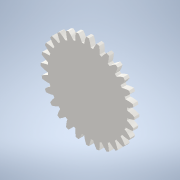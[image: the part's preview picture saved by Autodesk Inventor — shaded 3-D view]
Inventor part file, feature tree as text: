
AUTODESK INVENTOR PART (.ipt)
format: ipt  version: 2022 (Build 260153000, 153)  size: 248,320 bytes
history: native  units: mm (DEFAULTED — no unit token found)
features: plane x3, other x3, sketch x2, extrude x1
ambient origin geometry x8: Origin, YZ Plane, XZ Plane, XY Plane, X Axis, Y Axis, Z Axis, Center Point
bodies: Solid1 (feature_tree)
feature tree (9):
  extrude  "Extrusion1"  Depth=4.0mm TaperAngle=0.0deg
  plane  "Work Plane2"
  plane  "Work Plane8"
  plane  "Work Plane9"
  other  "Spur Gear"
  sketch  "Sketch1"  dims[d0=74.902823mm d1=4.0mm d2=0.0mm]
  sketch  "Sketch2"  dims[d3=70.0mm d4=10.0mm d5=0.0mm d16=70.971478mm d17=0.0mm d34=1.121997mm d39=0.0mm d41=0.0mm d43=70.971478mm d46=70.971478mm d47=0.0mm d48=0.0mm d49=6.5mm]
  other  "Srf1"
  other  "Pitch Diameter"
